annotation { "Feature Type Name" : "Feature", "Feature Type Description" : "" }
export const myFeature = defineFeature(function(context is Context, id is Id, definition is map)
    precondition{}
    {
        {
            var Q0;
            Q0=qCreatedBy(makeId("Front.planeOp"),FACE);
            var sketch = newSketch(context, id + "F0", { "sketchPlane" : qUnion([Q0])});
            skLineSegment(sketch, "E0.bottom", {"start": v(-50, 0) * mm, "end": v(50, 0) * mm});
            skLineSegment(sketch, "E0.top", {"start": v(-50, -100) * mm, "end": v(50, -100) * mm});
            skLineSegment(sketch, "E0.left", {"start": v(-50, 0) * mm, "end": v(-50, -100) * mm});
            skLineSegment(sketch, "E0.right", {"start": v(50, 0) * mm, "end": v(50, -100) * mm});
            skSolve(sketch);
        }
        {
            var Q0;
            Q0=makeQuery(id+"F0.imprint","IMPRINT",FACE,{"disambiguationData":[TD([[makeQuery(id+"F0.imprint","IMPRINT",EDGE,{"derivedFrom":sQuery(id+"F0.wireOp",EDGE,"E0.bottom")}),-1.0]])]});
            extrude(context, id + "F1", {"entities" : qUnion([Q0]), "depth" : 10 * mm, "offsetDistance" : 25 * mm});
        }
        {
            var Q0;
            Q0=qCreatedBy(makeId("Top.planeOp"),FACE);
            var sketch = newSketch(context, id + "F2", { "sketchPlane" : qUnion([Q0])});
            skLineSegment(sketch, "E1", {"start": v(-38, 0) * mm, "end": v(-7.7, 75) * mm});
            skLineSegment(sketch, "E2", {"start": v(-25, 0) * mm, "end": v(0, 61.88) * mm});
            skLineSegment(sketch, "E3", {"start": v(-27.86, 57.86) * mm, "end": v(-35.36, 50.36) * mm});
            skLineSegment(sketch, "E4", {"start": v(-35.36, 50.36) * mm, "end": v(0, 15) * mm});
            skLineSegment(sketch, "E5", {"start": v(-27.86, 57.86) * mm, "end": v(0, 30) * mm});
            skLineSegment(sketch, "E6", {"start": v(0, 0) * mm, "end": v(0, 5.32) * mm});
            skLineSegment(sketch, "E7.MirrorCS", {"start": v(25, 0) * mm, "end": v(0, 61.88) * mm});
            skLineSegment(sketch, "E8.MirrorCS", {"start": v(27.86, 57.86) * mm, "end": v(0, 30) * mm});
            skLineSegment(sketch, "E9.MirrorCS", {"start": v(35.36, 50.36) * mm, "end": v(0, 15) * mm});
            skLineSegment(sketch, "E10.MirrorCS", {"start": v(27.86, 57.86) * mm, "end": v(35.36, 50.36) * mm});
            skLineSegment(sketch, "E11.MirrorCS", {"start": v(38, 0) * mm, "end": v(7.7, 75) * mm});
            skLineSegment(sketch, "E12", {"start": v(-7.7, 75) * mm, "end": v(7.7, 75) * mm});
            skLineSegment(sketch, "E13", {"start": v(-38, 0) * mm, "end": v(-25, 0) * mm});
            skLineSegment(sketch, "E14", {"start": v(25, 0) * mm, "end": v(38, 0) * mm});
            skSolve(sketch);
        }
        {
            var Q0;
            Q0 = qSketchRegion(id + "F2", true);
            extrude(context, id + "F3", {"entities" : qUnion([Q0]), "oppositeDirection" : true, "depth" : 15 * mm, "offsetDistance" : 25 * mm});
        }
        {
            var Q0;
            Q0=makeQuery(id+"F1.opExtrude","CAP_FACE",FACE,{"disambiguationData":[OSD([sQuery(id+"F0.wireOp",EDGE,"E0.bottom"),sQuery(id+"F0.wireOp",EDGE,"E0.top"),sQuery(id+"F0.wireOp",EDGE,"E0.left"),sQuery(id+"F0.wireOp",EDGE,"E0.right")])],"isStart":true});
            var sketch = newSketch(context, id + "F4", { "sketchPlane" : qUnion([Q0])});
            skText(sketch, "E15", { "text": "ALLSTYLE DANCE\nBATTLE ACADEMY\nWINNER PRAGUE", "fontName": "OpenSans-Bold.ttf"});
            const initialGuessF4  = {"E15": [-0.04, -0.0665, 1, 0, 0.0065]};
            skSetInitialGuess(sketch, initialGuessF4);
            skSolve(sketch);
        }
        {
            var Q0;
            Q0 = qSketchRegion(id + "F4", true);
            extrude(context, id + "F5", {"entities" : qUnion([Q0]), "operationType" : NewBodyOperationType.REMOVE, "oppositeDirection" : true, "depth" : 2 * mm, "offsetDistance" : 25 * mm});
        }
    });